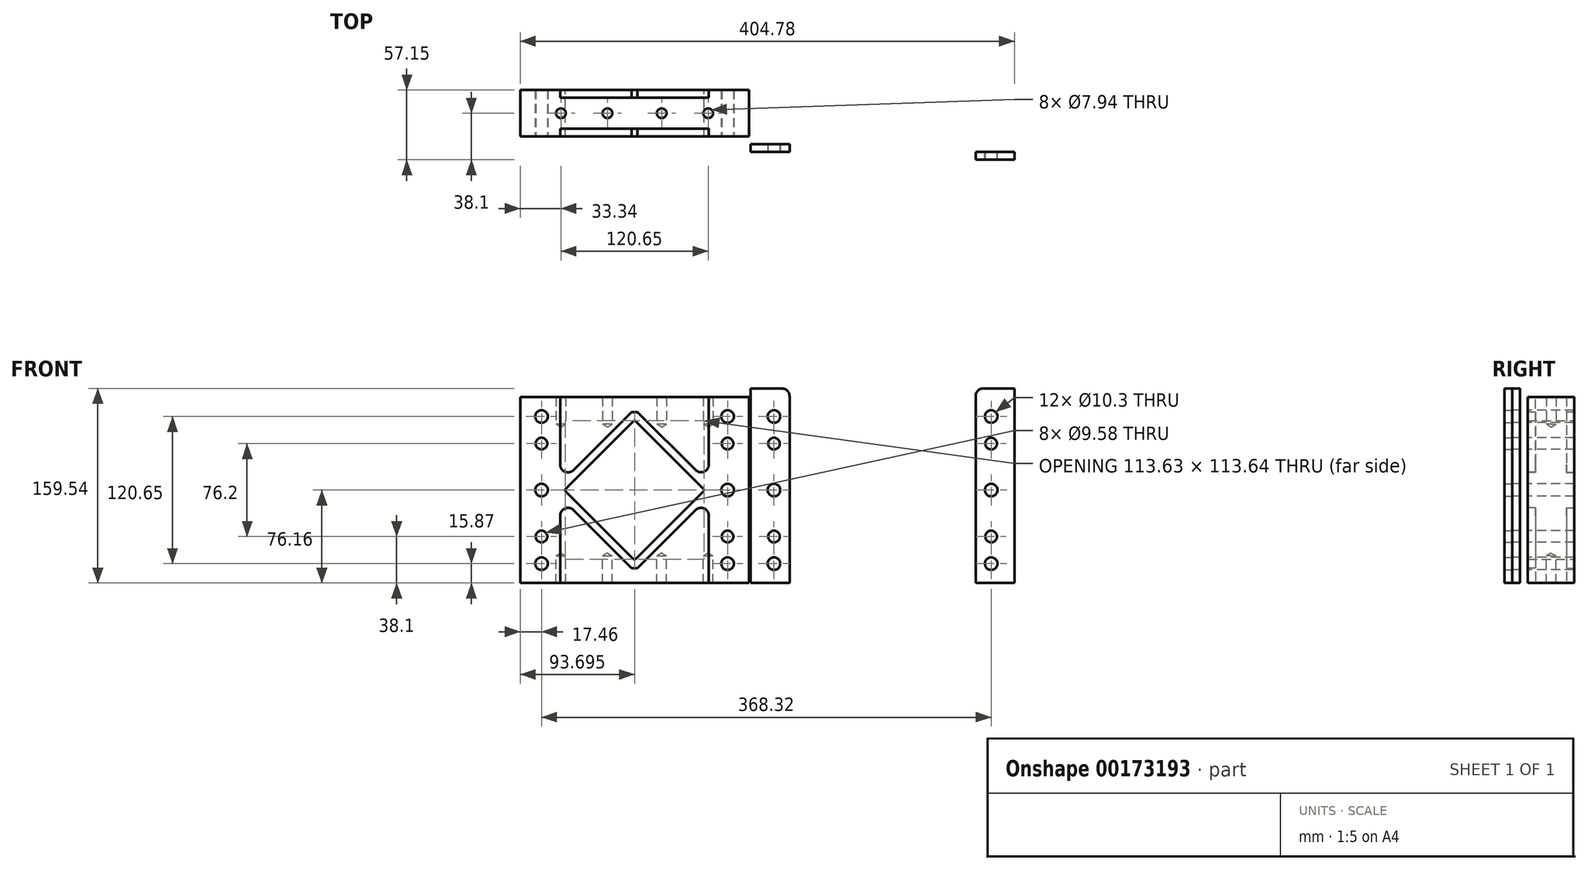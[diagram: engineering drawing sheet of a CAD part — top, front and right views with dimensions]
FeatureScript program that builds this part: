
annotation { "Feature Type Name" : "Feature", "Feature Type Description" : "" }
export const myFeature = defineFeature(function(context is Context, id is Id, definition is map)
    precondition{}
    {
        {
            var Q0;
            Q0=qCreatedBy(makeId("Front.planeOp"),FACE);
            var sketch = newSketch(context, id + "F0", { "sketchPlane" : qUnion([Q0])});
            skLineSegment(sketch, "E0.bottom", {"start": v(-76.3, 64.06) * mm, "end": v(111.02, 64.06) * mm});
            skLineSegment(sketch, "E0.top", {"start": v(-76.3, -88.34) * mm, "end": v(111.02, -88.34) * mm});
            skLineSegment(sketch, "E0.left", {"start": v(-76.3, 64.06) * mm, "end": v(-76.3, -88.34) * mm});
            skLineSegment(sketch, "E0.right", {"start": v(111.02, 64.06) * mm, "end": v(111.02, -88.34) * mm});
            skPoint(sketch, "E1", {"position": v(-58.84, -12.14) * mm});
            skPoint(sketch, "E2", {"position": v(-58.84, -50.24) * mm});
            skPoint(sketch, "E3", {"position": v(-58.84, -72.47) * mm});
            skPoint(sketch, "E4", {"position": v(-58.84, 25.96) * mm});
            skPoint(sketch, "E5", {"position": v(-58.84, 48.18) * mm});
            skPoint(sketch, "E6", {"position": v(93.56, 48.18) * mm});
            skPoint(sketch, "E7", {"position": v(93.56, 25.96) * mm});
            skPoint(sketch, "E8", {"position": v(93.56, -12.14) * mm});
            skPoint(sketch, "E9", {"position": v(93.56, -50.24) * mm});
            skPoint(sketch, "E10", {"position": v(93.56, -72.47) * mm});
            skPoint(sketch, "E11", {"position": v(17.4, -12.18) * mm});
            skLineSegment(sketch, "E12.0", {"start": v(73.75, -13.3) * mm, "end": v(18.52, -68.53) * mm});
            skLineSegment(sketch, "E13.0", {"start": v(-38.96, -13.3) * mm, "end": v(16.27, -68.53) * mm});
            skLineSegment(sketch, "E14.0", {"start": v(18.52, 44.17) * mm, "end": v(73.75, -11.06) * mm});
            skLineSegment(sketch, "E15.trimOffspring", {"start": v(16.27, 44.17) * mm, "end": v(-38.96, -11.06) * mm});
            skPoint(sketch, "E16.visualSharp", {"position": v(17.4, 45.3) * mm});
            skArc(sketch, "E16.filletArc", {"start": v(18.52, 44.17) * mm, "mid": v(17.4, 44.64) * mm, "end": v(16.27, 44.17) * mm});
            skPoint(sketch, "E17.visualSharp", {"position": v(74.87, -12.18) * mm});
            skArc(sketch, "E17.filletArc", {"start": v(73.75, -13.3) * mm, "mid": v(74.21, -12.18) * mm, "end": v(73.75, -11.06) * mm});
            skPoint(sketch, "E18.visualSharp", {"position": v(17.4, -69.65) * mm});
            skArc(sketch, "E18.filletArc", {"start": v(16.27, -68.53) * mm, "mid": v(17.4, -69) * mm, "end": v(18.52, -68.53) * mm});
            skPoint(sketch, "E19.visualSharp", {"position": v(-40.08, -12.18) * mm});
            skArc(sketch, "E19.filletArc", {"start": v(-38.96, -11.06) * mm, "mid": v(-39.42, -12.18) * mm, "end": v(-38.96, -13.3) * mm});
            skSolve(sketch);
        }
        {
            var Q0;
            Q0=makeQuery(id+"F0.imprint","IMPRINT",FACE,{"disambiguationData":[TD([[makeQuery(id+"F0.imprint","IMPRINT",EDGE,{"derivedFrom":sQuery(id+"F0.wireOp",EDGE,"E0.bottom")}),-1.0]])]});
            extrude(context, id + "F1", {"entities" : qUnion([Q0]), "depth" : 38.1 * mm});
        }
        {
            var Q0;
            Q0=makeQuery(id+"F1.opExtrude","CAP_FACE",FACE,{"disambiguationData":[OSD([sQuery(id+"F0.wireOp",EDGE,"E0.bottom"),sQuery(id+"F0.wireOp",EDGE,"E0.top"),sQuery(id+"F0.wireOp",EDGE,"E0.left"),sQuery(id+"F0.wireOp",EDGE,"E0.right"),sQuery(id+"F0.wireOp",EDGE,"9NI2HCdm-zhV7-IXKU-Ilw0-qgHgseYNw8uk"),sQuery(id+"F0.wireOp",EDGE,"780ab442-0033-43c3-96a2-e75c31360361"),sQuery(id+"F0.wireOp",EDGE,"ca78d6b7-7b32-4318-8b30-639c1e3c6c27"),sQuery(id+"F0.wireOp",EDGE,"23cbe407-0eed-4e64-8f3f-165a4f1e2653"),sQuery(id+"F0.wireOp",EDGE,"2d58fa3e-12f2-48dd-afb8-51d7db77980c"),sQuery(id+"F0.wireOp",EDGE,"b4ce7634-13e8-413b-b57b-a0738a6edea7"),sQuery(id+"F0.wireOp",EDGE,"E12.0"),sQuery(id+"F0.wireOp",EDGE,"E13.0"),sQuery(id+"F0.wireOp",EDGE,"E14.0"),sQuery(id+"F0.wireOp",EDGE,"E15.trimOffspring"),sQuery(id+"F0.wireOp",EDGE,"E16.filletArc"),sQuery(id+"F0.wireOp",EDGE,"E17.filletArc"),sQuery(id+"F0.wireOp",EDGE,"E18.filletArc"),sQuery(id+"F0.wireOp",EDGE,"E19.filletArc")])],"isStart":false});
            var sketch = newSketch(context, id + "F2", { "sketchPlane" : qUnion([Q0])});
            skLineSegment(sketch, "E20.0", {"start": v(14.96, 51.84) * mm, "end": v(-32.67, 4.2) * mm});
            skLineSegment(sketch, "E21.0", {"start": v(19.83, 51.84) * mm, "end": v(67.4, 4.28) * mm});
            skLineSegment(sketch, "E22.0", {"start": v(67.4, -28.63) * mm, "end": v(19.83, -76.2) * mm});
            skLineSegment(sketch, "E23.0", {"start": v(-32.67, -28.56) * mm, "end": v(14.96, -76.2) * mm});
            skLineSegment(sketch, "E24", {"start": v(78.24, 8.77) * mm, "end": v(78.24, 64.06) * mm});
            skLineSegment(sketch, "E25", {"start": v(78.24, -33.12) * mm, "end": v(78.24, -88.34) * mm});
            skLineSegment(sketch, "E26", {"start": v(-76.3, -12.14) * mm, "end": v(111.02, -12.14) * mm});
            skLineSegment(sketch, "E27", {"start": v(17.36, -12.14) * mm, "end": v(17.35, -88.34) * mm});
            skLineSegment(sketch, "E28", {"start": v(17.36, -12.14) * mm, "end": v(17.36, 64.06) * mm});
            skLineSegment(sketch, "E29.MirrorCS", {"start": v(-43.51, 8.7) * mm, "end": v(-43.51, 64.06) * mm});
            skLineSegment(sketch, "E30.MirrorCS", {"start": v(-43.51, -33.05) * mm, "end": v(-43.51, -88.34) * mm});
            skPoint(sketch, "E31.newPointB", {"position": v(-43.51, -6.56) * mm});
            skArc(sketch, "E31.filletArc", {"start": v(-43.51, 8.7) * mm, "mid": v(-39.6, 2.83) * mm, "end": v(-32.67, 4.2) * mm});
            skPoint(sketch, "E32.newPointB", {"position": v(-43.51, -17.8) * mm});
            skArc(sketch, "E32.filletArc", {"start": v(-32.67, -28.56) * mm, "mid": v(-39.6, -27.19) * mm, "end": v(-43.51, -33.05) * mm});
            skPoint(sketch, "E33.visualSharp", {"position": v(78.24, -17.8) * mm});
            skArc(sketch, "E33.filletArc", {"start": v(78.24, -33.12) * mm, "mid": v(74.32, -27.25) * mm, "end": v(67.4, -28.63) * mm});
            skLineSegment(sketch, "E34.0", {"start": v(14.96, 51.84) * mm, "end": v(19.83, 51.84) * mm});
            skPoint(sketch, "E35.orphan", {"position": v(23, 48.66) * mm});
            skLineSegment(sketch, "E36.0", {"start": v(19.83, -76.2) * mm, "end": v(14.96, -76.2) * mm});
            skPoint(sketch, "E37.visualSharp", {"position": v(78.24, -6.56) * mm});
            skArc(sketch, "E37.filletArc", {"start": v(67.4, 4.28) * mm, "mid": v(74.32, 2.9) * mm, "end": v(78.24, 8.77) * mm});
            skLineSegment(sketch, "E38", {"start": v(19.83, 51.84) * mm, "end": v(14.96, 51.84) * mm});
            skLineSegment(sketch, "E39", {"start": v(14.96, -76.2) * mm, "end": v(19.83, -76.2) * mm});
            skSolve(sketch);
        }
        {
            var Q0;
            Q0=sQuery(id+"F0.wireOp",VERTEX,"E4");
            var Q1;
            Q1=sQuery(id+"F0.wireOp",VERTEX,"E2");
            var Q2;
            Q2=sQuery(id+"F0.wireOp",VERTEX,"E9");
            var Q3;
            Q3=sQuery(id+"F0.wireOp",VERTEX,"E7");
            var Q4;
            Q4=makeQuery(id+"F1.opExtrude","SWEPT_BODY",BODY,{"disambiguationData":[OSD([sQuery(id+"F0.wireOp",EDGE,"E0.bottom"),sQuery(id+"F0.wireOp",EDGE,"E0.top"),sQuery(id+"F0.wireOp",EDGE,"E0.left"),sQuery(id+"F0.wireOp",EDGE,"E0.right"),sQuery(id+"F0.wireOp",EDGE,"9NI2HCdm-zhV7-IXKU-Ilw0-qgHgseYNw8uk"),sQuery(id+"F0.wireOp",EDGE,"780ab442-0033-43c3-96a2-e75c31360361"),sQuery(id+"F0.wireOp",EDGE,"ca78d6b7-7b32-4318-8b30-639c1e3c6c27"),sQuery(id+"F0.wireOp",EDGE,"23cbe407-0eed-4e64-8f3f-165a4f1e2653"),sQuery(id+"F0.wireOp",EDGE,"2d58fa3e-12f2-48dd-afb8-51d7db77980c"),sQuery(id+"F0.wireOp",EDGE,"b4ce7634-13e8-413b-b57b-a0738a6edea7"),sQuery(id+"F0.wireOp",EDGE,"E12.0"),sQuery(id+"F0.wireOp",EDGE,"E13.0"),sQuery(id+"F0.wireOp",EDGE,"E14.0"),sQuery(id+"F0.wireOp",EDGE,"E15.trimOffspring"),sQuery(id+"F0.wireOp",EDGE,"E16.filletArc"),sQuery(id+"F0.wireOp",EDGE,"E17.filletArc"),sQuery(id+"F0.wireOp",EDGE,"E18.filletArc"),sQuery(id+"F0.wireOp",EDGE,"E19.filletArc")])]});
            hole(context, id + "F3", {"style" : HoleStyle.SIMPLE, "endStyle" : HoleEndStyle.THROUGH, "oppositeDirection" : true, "holeDiameter" : 9.58 * mm, "locations" : qUnion([Q0, Q1, Q2, Q3]), "scope" : qUnion([Q4]), "isTappedThrough" : true});
        }
        {
            var Q0;
            {var subQ6=sQuery(id+"F2.wireOp",EDGE,"E20.0");Q0=makeQuery(id+"F2.imprint","IMPRINT",FACE,{"disambiguationData":[TD([[makeQuery(id+"F2.imprint","IMPRINT",EDGE,{"derivedFrom":subQ6}),-1.0]])]});}
            var Q1;
            {var subQ1=sQuery(id+"F2.wireOp",EDGE,"E21.0");Q1=makeQuery(id+"F2.imprint","IMPRINT",FACE,{"disambiguationData":[TD([[makeQuery(id+"F2.imprint","IMPRINT",EDGE,{"derivedFrom":subQ1}),1.0]])]});}
            var Q2;
            {var subQ6=sQuery(id+"F2.wireOp",EDGE,"E22.0");Q2=makeQuery(id+"F2.imprint","IMPRINT",FACE,{"disambiguationData":[TD([[makeQuery(id+"F2.imprint","IMPRINT",EDGE,{"derivedFrom":subQ6}),1.0]])]});}
            var Q3;
            {var subQ6=sQuery(id+"F2.wireOp",EDGE,"E23.0");Q3=makeQuery(id+"F2.imprint","IMPRINT",FACE,{"disambiguationData":[TD([[makeQuery(id+"F2.imprint","IMPRINT",EDGE,{"derivedFrom":subQ6}),-1.0]])]});}
            extrude(context, id + "F4", {"entities" : qUnion([Q0, Q1, Q2, Q3]), "operationType" : NewBodyOperationType.REMOVE, "oppositeDirection" : true, "depth" : 6.35 * mm});
        }
        {
            var Q0;
            Q0=makeQuery(id+"F0.imprint","IMPRINT",FACE,{"disambiguationData":[TD([[makeQuery(id+"F0.imprint","IMPRINT",EDGE,{"derivedFrom":sQuery(id+"F0.wireOp",EDGE,"E0.bottom")}),-1.0]])]});
            var sketch = newSketch(context, id + "F5", { "sketchPlane" : qUnion([Q0])});
            skLineSegment(sketch, "E40.0", {"start": v(19.76, 51.91) * mm, "end": v(67.4, 4.28) * mm});
            skLineSegment(sketch, "E41.0", {"start": v(15.03, 51.91) * mm, "end": v(-32.67, 4.21) * mm});
            skLineSegment(sketch, "E42.0", {"start": v(-32.67, -28.57) * mm, "end": v(14.97, -76.2) * mm});
            skLineSegment(sketch, "E43.0", {"start": v(67.4, -28.63) * mm, "end": v(19.82, -76.2) * mm});
            skLineSegment(sketch, "E44.0", {"start": v(78.23, 64.06) * mm, "end": v(78.23, 8.77) * mm});
            skLineSegment(sketch, "E45.0", {"start": v(-43.5, 64.06) * mm, "end": v(-43.5, 8.7) * mm});
            skLineSegment(sketch, "E46.0", {"start": v(-76.3, 51.91) * mm, "end": v(-43.5, 51.91) * mm});
            skLineSegment(sketch, "E47.trimOffspring", {"start": v(15.03, 51.91) * mm, "end": v(19.76, 51.91) * mm});
            skLineSegment(sketch, "E48.trimOffspring", {"start": v(14.97, -76.2) * mm, "end": v(19.82, -76.2) * mm});
            skLineSegment(sketch, "E49.trimOffspring", {"start": v(78.23, -76.2) * mm, "end": v(111.02, -76.2) * mm});
            skArc(sketch, "E50.filletArc", {"start": v(67.4, 4.28) * mm, "mid": v(74.31, 2.9) * mm, "end": v(78.23, 8.77) * mm});
            skArc(sketch, "E51.filletArc", {"start": v(-43.5, 8.7) * mm, "mid": v(-39.59, 2.84) * mm, "end": v(-32.67, 4.21) * mm});
            skLineSegment(sketch, "E52", {"start": v(-43.5, 8.7) * mm, "end": v(-43.5, 2.84) * mm});
            skPoint(sketch, "E52.endSnap0", {"position": v(-39.59, 2.84) * mm});
            skLineSegment(sketch, "E53", {"start": v(78.23, -33.12) * mm, "end": v(78.23, -90.42) * mm});
            skLineSegment(sketch, "E54", {"start": v(-43.5, -33.06) * mm, "end": v(-43.5, -90.42) * mm});
            skPoint(sketch, "E55.newPointB", {"position": v(78.23, 8.77) * mm});
            skArc(sketch, "E55.filletArc", {"start": v(78.23, -33.12) * mm, "mid": v(74.31, -27.26) * mm, "end": v(67.4, -28.63) * mm});
            skArc(sketch, "E56.filletArc", {"start": v(-32.67, -28.57) * mm, "mid": v(-39.59, -27.2) * mm, "end": v(-43.5, -33.06) * mm});
            skSolve(sketch);
        }
        {
            var Q0;
            Q0=makeQuery(id+"F5.imprint","IMPRINT",FACE,{"disambiguationData":[TD([[makeQuery(id+"F5.imprint","IMPRINT",EDGE,{"derivedFrom":sQuery(id+"F5.wireOp",EDGE,"E42.0")}),-1.0]])]});
            var Q1;
            Q1=makeQuery(id+"F5.imprint","IMPRINT",FACE,{"disambiguationData":[TD([[makeQuery(id+"F5.imprint","IMPRINT",EDGE,{"derivedFrom":sQuery(id+"F5.wireOp",EDGE,"E40.0")}),1.0]])]});
            extrude(context, id + "F6", {"entities" : qUnion([Q0, Q1]), "operationType" : NewBodyOperationType.REMOVE, "depth" : 6.35 * mm});
        }
        {
            var Q0;
            Q0=makeQuery(id+"F1.opExtrude","SWEPT_FACE",FACE,{"disambiguationData":[OSD([sQuery(id+"F0.wireOp",EDGE,"E0.top")])]});
            var sketch = newSketch(context, id + "F7", { "sketchPlane" : qUnion([Q0])});
            skLineSegment(sketch, "E57", {"start": v(-76.3, 19.05) * mm, "end": v(111.02, 19.05) * mm});
            skPoint(sketch, "E58.endSnap0", {"position": v(17.36, 31.75) * mm});
            skLineSegment(sketch, "E59", {"start": v(17.36, 6.35) * mm, "end": v(17.36, 31.75) * mm});
            skLineSegment(sketch, "E60.0", {"start": v(39.59, 6.35) * mm, "end": v(39.59, 31.75) * mm});
            skLineSegment(sketch, "E61.0", {"start": v(-4.86, 6.35) * mm, "end": v(-4.86, 31.75) * mm});
            skLineSegment(sketch, "E62.0", {"start": v(77.69, 6.35) * mm, "end": v(77.69, 31.75) * mm});
            skLineSegment(sketch, "E63.0", {"start": v(71.88, -6.35) * mm, "end": v(71.88, 0) * mm});
            skLineSegment(sketch, "E63.1", {"start": v(-82.65, 44.45) * mm, "end": v(-37.16, 44.45) * mm});
            skLineSegment(sketch, "E63.2", {"start": v(-82.65, -6.35) * mm, "end": v(-82.65, 44.45) * mm});
            skLineSegment(sketch, "E63.3", {"start": v(-37.16, -6.35) * mm, "end": v(-82.65, -6.35) * mm});
            skLineSegment(sketch, "E63.4", {"start": v(-37.16, 0) * mm, "end": v(-37.16, -6.35) * mm});
            skLineSegment(sketch, "E63.5", {"start": v(-37.16, 44.45) * mm, "end": v(-37.16, 38.1) * mm});
            skLineSegment(sketch, "E63.6", {"start": v(71.88, 0) * mm, "end": v(-37.16, 0) * mm});
            skLineSegment(sketch, "E63.7", {"start": v(-37.16, 38.1) * mm, "end": v(71.89, 38.1) * mm});
            skLineSegment(sketch, "E63.8", {"start": v(71.89, 38.1) * mm, "end": v(71.89, 44.45) * mm});
            skLineSegment(sketch, "E63.9", {"start": v(71.89, 44.45) * mm, "end": v(117.37, 44.45) * mm});
            skLineSegment(sketch, "E63.10", {"start": v(117.37, 44.45) * mm, "end": v(117.37, -6.35) * mm});
            skLineSegment(sketch, "E63.11", {"start": v(117.37, -6.35) * mm, "end": v(71.88, -6.35) * mm});
            skLineSegment(sketch, "E64.0", {"start": v(-42.96, 6.35) * mm, "end": v(-42.96, 31.75) * mm});
            skPoint(sketch, "E65", {"position": v(-42.96, 19.05) * mm});
            skPoint(sketch, "E66", {"position": v(-4.86, 19.05) * mm});
            skPoint(sketch, "E67", {"position": v(39.59, 19.05) * mm});
            skPoint(sketch, "E68", {"position": v(77.69, 19.05) * mm});
            skSolve(sketch);
        }
        {
            var Q0;
            Q0=sQuery(id+"F7.wireOp",VERTEX,"E65");
            var Q1;
            Q1=sQuery(id+"F7.wireOp",VERTEX,"E66");
            var Q2;
            Q2=sQuery(id+"F7.wireOp",VERTEX,"E68");
            var Q3;
            Q3=sQuery(id+"F7.wireOp",VERTEX,"E67");
            var Q4;
            Q4=makeQuery(id+"F1.opExtrude","SWEPT_BODY",BODY,{"disambiguationData":[OSD([sQuery(id+"F0.wireOp",EDGE,"E0.bottom"),sQuery(id+"F0.wireOp",EDGE,"E0.top"),sQuery(id+"F0.wireOp",EDGE,"E0.left"),sQuery(id+"F0.wireOp",EDGE,"E0.right"),sQuery(id+"F0.wireOp",EDGE,"9NI2HCdm-zhV7-IXKU-Ilw0-qgHgseYNw8uk"),sQuery(id+"F0.wireOp",EDGE,"780ab442-0033-43c3-96a2-e75c31360361"),sQuery(id+"F0.wireOp",EDGE,"ca78d6b7-7b32-4318-8b30-639c1e3c6c27"),sQuery(id+"F0.wireOp",EDGE,"23cbe407-0eed-4e64-8f3f-165a4f1e2653"),sQuery(id+"F0.wireOp",EDGE,"2d58fa3e-12f2-48dd-afb8-51d7db77980c"),sQuery(id+"F0.wireOp",EDGE,"b4ce7634-13e8-413b-b57b-a0738a6edea7"),sQuery(id+"F0.wireOp",EDGE,"E12.0"),sQuery(id+"F0.wireOp",EDGE,"E13.0"),sQuery(id+"F0.wireOp",EDGE,"E14.0"),sQuery(id+"F0.wireOp",EDGE,"E15.trimOffspring"),sQuery(id+"F0.wireOp",EDGE,"E16.filletArc"),sQuery(id+"F0.wireOp",EDGE,"E17.filletArc"),sQuery(id+"F0.wireOp",EDGE,"E18.filletArc"),sQuery(id+"F0.wireOp",EDGE,"E19.filletArc")])]});
            hole(context, id + "F8", {"style" : HoleStyle.SIMPLE, "endStyle" : HoleEndStyle.BLIND, "holeDiameter" : 7.94 * mm, "holeDepth" : 22.22 * mm, "locations" : qUnion([Q0, Q1, Q2, Q3]), "scope" : qUnion([Q4])});
        }
        {
            var Q0;
            Q0=makeQuery(id+"F1.opExtrude","SWEPT_FACE",FACE,{"disambiguationData":[OSD([sQuery(id+"F0.wireOp",EDGE,"E0.bottom")])]});
            var sketch = newSketch(context, id + "F9", { "sketchPlane" : qUnion([Q0])});
            skLineSegment(sketch, "E69", {"start": v(-76.3, -19.05) * mm, "end": v(111.02, -19.05) * mm});
            skLineSegment(sketch, "E70", {"start": v(17.36, -30.06) * mm, "end": v(17.36, -6.35) * mm});
            skPoint(sketch, "E70.startSnap0", {"position": v(17.36, -31.75) * mm});
            skLineSegment(sketch, "E71", {"start": v(39.59, -6.35) * mm, "end": v(39.59, -31.75) * mm});
            skLineSegment(sketch, "E72", {"start": v(-4.86, -6.35) * mm, "end": v(-4.86, -31.75) * mm});
            skLineSegment(sketch, "E73", {"start": v(77.69, -6.35) * mm, "end": v(77.69, -31.75) * mm});
            skLineSegment(sketch, "E74", {"start": v(-42.96, -31.75) * mm, "end": v(-42.96, -6.35) * mm});
            skPoint(sketch, "E75", {"position": v(77.69, -19.05) * mm});
            skPoint(sketch, "E76", {"position": v(39.59, -19.05) * mm});
            skPoint(sketch, "E77", {"position": v(-4.86, -19.05) * mm});
            skPoint(sketch, "E78", {"position": v(-42.96, -19.05) * mm});
            skSolve(sketch);
        }
        {
            var Q0;
            Q0=sQuery(id+"F9.wireOp",VERTEX,"E78");
            var Q1;
            Q1=sQuery(id+"F9.wireOp",VERTEX,"E77");
            var Q2;
            Q2=sQuery(id+"F9.wireOp",VERTEX,"E76");
            var Q3;
            Q3=sQuery(id+"F9.wireOp",VERTEX,"E75");
            var Q4;
            Q4=makeQuery(id+"F1.opExtrude","SWEPT_BODY",BODY,{"disambiguationData":[OSD([sQuery(id+"F0.wireOp",EDGE,"E0.bottom"),sQuery(id+"F0.wireOp",EDGE,"E0.top"),sQuery(id+"F0.wireOp",EDGE,"E0.left"),sQuery(id+"F0.wireOp",EDGE,"E0.right"),sQuery(id+"F0.wireOp",EDGE,"9NI2HCdm-zhV7-IXKU-Ilw0-qgHgseYNw8uk"),sQuery(id+"F0.wireOp",EDGE,"780ab442-0033-43c3-96a2-e75c31360361"),sQuery(id+"F0.wireOp",EDGE,"ca78d6b7-7b32-4318-8b30-639c1e3c6c27"),sQuery(id+"F0.wireOp",EDGE,"23cbe407-0eed-4e64-8f3f-165a4f1e2653"),sQuery(id+"F0.wireOp",EDGE,"2d58fa3e-12f2-48dd-afb8-51d7db77980c"),sQuery(id+"F0.wireOp",EDGE,"b4ce7634-13e8-413b-b57b-a0738a6edea7"),sQuery(id+"F0.wireOp",EDGE,"E12.0"),sQuery(id+"F0.wireOp",EDGE,"E13.0"),sQuery(id+"F0.wireOp",EDGE,"E14.0"),sQuery(id+"F0.wireOp",EDGE,"E15.trimOffspring"),sQuery(id+"F0.wireOp",EDGE,"E16.filletArc"),sQuery(id+"F0.wireOp",EDGE,"E17.filletArc"),sQuery(id+"F0.wireOp",EDGE,"E18.filletArc"),sQuery(id+"F0.wireOp",EDGE,"E19.filletArc")])]});
            hole(context, id + "F10", {"style" : HoleStyle.SIMPLE, "endStyle" : HoleEndStyle.BLIND, "holeDiameter" : 7.94 * mm, "holeDepth" : 22.22 * mm, "locations" : qUnion([Q0, Q1, Q2, Q3]), "scope" : qUnion([Q4])});
        }
        {
            var Q0;
            Q0=sQuery(id+"F0.wireOp",VERTEX,"E3");
            var Q1;
            Q1=sQuery(id+"F0.wireOp",VERTEX,"E1");
            var Q2;
            Q2=sQuery(id+"F0.wireOp",VERTEX,"E5");
            var Q3;
            Q3=sQuery(id+"F0.wireOp",VERTEX,"E6");
            var Q4;
            Q4=sQuery(id+"F0.wireOp",VERTEX,"E8");
            var Q5;
            Q5=sQuery(id+"F0.wireOp",VERTEX,"E10");
            var Q6;
            Q6=makeQuery(id+"F1.opExtrude","SWEPT_BODY",BODY,{"disambiguationData":[OSD([sQuery(id+"F0.wireOp",EDGE,"E0.bottom"),sQuery(id+"F0.wireOp",EDGE,"E0.top"),sQuery(id+"F0.wireOp",EDGE,"E0.left"),sQuery(id+"F0.wireOp",EDGE,"E0.right"),sQuery(id+"F0.wireOp",EDGE,"E12.0"),sQuery(id+"F0.wireOp",EDGE,"E13.0"),sQuery(id+"F0.wireOp",EDGE,"E14.0"),sQuery(id+"F0.wireOp",EDGE,"E15.trimOffspring"),sQuery(id+"F0.wireOp",EDGE,"E16.filletArc"),sQuery(id+"F0.wireOp",EDGE,"E17.filletArc"),sQuery(id+"F0.wireOp",EDGE,"E18.filletArc"),sQuery(id+"F0.wireOp",EDGE,"E19.filletArc")])]});
            hole(context, id + "F11", {"style" : HoleStyle.SIMPLE, "endStyle" : HoleEndStyle.THROUGH, "oppositeDirection" : true, "holeDiameter" : 10.3 * mm, "locations" : qUnion([Q0, Q1, Q2, Q3, Q4, Q5]), "scope" : qUnion([Q6]), "isTappedThrough" : true});
        }
        {
            var Q0;
            Q0=makeQuery(id+"F1.opExtrude","CAP_FACE",FACE,{"disambiguationData":[OSD([sQuery(id+"F0.wireOp",EDGE,"E0.bottom"),sQuery(id+"F0.wireOp",EDGE,"E0.top"),sQuery(id+"F0.wireOp",EDGE,"E0.left"),sQuery(id+"F0.wireOp",EDGE,"E0.right"),sQuery(id+"F0.wireOp",EDGE,"E12.0"),sQuery(id+"F0.wireOp",EDGE,"E13.0"),sQuery(id+"F0.wireOp",EDGE,"E14.0"),sQuery(id+"F0.wireOp",EDGE,"E15.trimOffspring"),sQuery(id+"F0.wireOp",EDGE,"E16.filletArc"),sQuery(id+"F0.wireOp",EDGE,"E17.filletArc"),sQuery(id+"F0.wireOp",EDGE,"E18.filletArc"),sQuery(id+"F0.wireOp",EDGE,"E19.filletArc")])],"isStart":false});
            var sketch = newSketch(context, id + "F12", { "sketchPlane" : qUnion([Q0])});
            skLineSegment(sketch, "E79", {"start": v(17.4, 51.84) * mm, "end": v(17.4, -69) * mm});
            skLineSegment(sketch, "E80.0", {"start": v(17.3, 51.84) * mm, "end": v(17.3, -69) * mm});
            skLineSegment(sketch, "E81.0", {"start": v(-46.2, 51.84) * mm, "end": v(-46.2, -69) * mm});
            skLineSegment(sketch, "E82.0", {"start": v(80.8, 51.84) * mm, "end": v(80.8, -69) * mm});
            skLineSegment(sketch, "E83.top", {"start": v(87.16, 71.2) * mm, "end": v(112.56, 71.2) * mm});
            skLineSegment(sketch, "E83.left", {"start": v(80.8, -8.58) * mm, "end": v(80.8, 64.85) * mm});
            skLineSegment(sketch, "E83.right", {"start": v(112.56, -8.58) * mm, "end": v(112.56, 71.2) * mm});
            skLineSegment(sketch, "E84.top", {"start": v(80.8, -88.34) * mm, "end": v(112.56, -88.34) * mm});
            skLineSegment(sketch, "E84.left", {"start": v(80.8, -8.58) * mm, "end": v(80.8, -88.34) * mm});
            skLineSegment(sketch, "E84.right", {"start": v(112.56, -8.58) * mm, "end": v(112.56, -88.34) * mm});
            skPoint(sketch, "E85.visualSharp", {"position": v(80.8, 71.2) * mm});
            skArc(sketch, "E85.filletArc", {"start": v(87.16, 71.2) * mm, "mid": v(82.67, 69.34) * mm, "end": v(80.8, 64.85) * mm});
            skSolve(sketch);
        }
        {
            var Q0;
            {var subQ0=sQuery(id+"F0.wireOp",EDGE,"E0.right");var subQ8=makeQuery(id+"F1.opExtrude","CAP_EDGE",EDGE,{"disambiguationData":[OSD([subQ0])],"isStart":false});Q0=makeQuery(id+"F12.imprint","IMPRINT",FACE,{"disambiguationData":[TD([[makeQuery(id+"F12.imprint","IMPRINT",EDGE,{"derivedFrom":subQ8}),-1.0]])]});}
            var Q1;
            Q1=makeQuery(id+"F12.imprint","IMPRINT",FACE,{"disambiguationData":[TD([[makeQuery(id+"F12.imprint","IMPRINT",EDGE,{"derivedFrom":sQuery(id+"F12.wireOp",EDGE,"E83.top")}),-1.0]])]});
            extrude(context, id + "F13", {"entities" : qUnion([Q0, Q1]), "depth" : 6.35 * mm});
        }
        {
            var Q0;
            Q0=makeQuery(id+"F13.opExtrude","SWEPT_BODY",BODY,{"disambiguationData":[OSD([sQuery(id+"F0.wireOp",EDGE,"E0.bottom"),sQuery(id+"F0.wireOp",EDGE,"E0.top"),sQuery(id+"F0.wireOp",EDGE,"E0.left"),sQuery(id+"F0.wireOp",EDGE,"E0.right"),sQuery(id+"F0.wireOp",EDGE,"E12.0"),sQuery(id+"F0.wireOp",EDGE,"E13.0"),sQuery(id+"F0.wireOp",EDGE,"E14.0"),sQuery(id+"F0.wireOp",EDGE,"E15.trimOffspring"),sQuery(id+"F0.wireOp",EDGE,"E16.filletArc"),sQuery(id+"F0.wireOp",EDGE,"E17.filletArc"),sQuery(id+"F0.wireOp",EDGE,"E18.filletArc"),sQuery(id+"F0.wireOp",EDGE,"E19.filletArc"),sQuery(id+"F3.hole-2.sketch.wireOp",EDGE,"core_line_2"),sQuery(id+"F3.hole-3.sketch.wireOp",EDGE,"core_line_2"),sQuery(id+"F11.hole-3.sketch.wireOp",EDGE,"core_line_2"),sQuery(id+"F11.hole-4.sketch.wireOp",EDGE,"core_line_2"),sQuery(id+"F11.hole-5.sketch.wireOp",EDGE,"core_line_2"),sQuery(id+"F12.wireOp",EDGE,"E83.top"),sQuery(id+"F12.wireOp",EDGE,"E83.left"),sQuery(id+"F12.wireOp",EDGE,"E83.right"),sQuery(id+"F12.wireOp",EDGE,"E84.top"),sQuery(id+"F12.wireOp",EDGE,"E84.left"),sQuery(id+"F12.wireOp",EDGE,"E84.right"),sQuery(id+"F12.wireOp",EDGE,"E85.filletArc")])]});
            var Q1;
            Q1=makeQuery(id+"F13.opExtrude","CAP_EDGE",EDGE,{"disambiguationData":[OSD([sQuery(id+"F12.wireOp",EDGE,"E83.right"),sQuery(id+"F12.wireOp",EDGE,"E84.right")])],"isStart":false});
            transform(context, id + "F14", {"entities" : qUnion([Q0]), "transformType" : TransformType.ROTATION, "transformAxis" : qUnion([Q1]), "angle" : 180 * degree, "makeCopy" : false});
        }
        {
            var Q0;
            Q0=makeQuery(id+"F13.opExtrude","SWEPT_BODY",BODY,{"disambiguationData":[OSD([sQuery(id+"F0.wireOp",EDGE,"E0.bottom"),sQuery(id+"F0.wireOp",EDGE,"E0.top"),sQuery(id+"F0.wireOp",EDGE,"E0.left"),sQuery(id+"F0.wireOp",EDGE,"E0.right"),sQuery(id+"F0.wireOp",EDGE,"E12.0"),sQuery(id+"F0.wireOp",EDGE,"E13.0"),sQuery(id+"F0.wireOp",EDGE,"E14.0"),sQuery(id+"F0.wireOp",EDGE,"E15.trimOffspring"),sQuery(id+"F0.wireOp",EDGE,"E16.filletArc"),sQuery(id+"F0.wireOp",EDGE,"E17.filletArc"),sQuery(id+"F0.wireOp",EDGE,"E18.filletArc"),sQuery(id+"F0.wireOp",EDGE,"E19.filletArc"),sQuery(id+"F3.hole-2.sketch.wireOp",EDGE,"core_line_2"),sQuery(id+"F3.hole-3.sketch.wireOp",EDGE,"core_line_2"),sQuery(id+"F11.hole-3.sketch.wireOp",EDGE,"core_line_2"),sQuery(id+"F11.hole-4.sketch.wireOp",EDGE,"core_line_2"),sQuery(id+"F11.hole-5.sketch.wireOp",EDGE,"core_line_2"),sQuery(id+"F12.wireOp",EDGE,"E83.top"),sQuery(id+"F12.wireOp",EDGE,"E83.left"),sQuery(id+"F12.wireOp",EDGE,"E83.right"),sQuery(id+"F12.wireOp",EDGE,"E84.top"),sQuery(id+"F12.wireOp",EDGE,"E84.left"),sQuery(id+"F12.wireOp",EDGE,"E84.right"),sQuery(id+"F12.wireOp",EDGE,"E85.filletArc")])]});
            transform(context, id + "F15", {"entities" : qUnion([Q0]), "transformType" : TransformType.TRANSLATION_3D, "dx" : 152.4 * mm, "dy" : 0 * mm, "dz" : 0 * mm, "makeCopy" : true});
        }
        {
            var Q0;
            Q0=makeQuery(id+"F15.opPattern","COPY",BODY,{"derivedFrom":makeQuery(id+"F13.opExtrude","SWEPT_BODY",BODY,{"disambiguationData":[OSD([sQuery(id+"F0.wireOp",EDGE,"E0.bottom"),sQuery(id+"F0.wireOp",EDGE,"E0.top"),sQuery(id+"F0.wireOp",EDGE,"E0.left"),sQuery(id+"F0.wireOp",EDGE,"E0.right"),sQuery(id+"F0.wireOp",EDGE,"E12.0"),sQuery(id+"F0.wireOp",EDGE,"E13.0"),sQuery(id+"F0.wireOp",EDGE,"E14.0"),sQuery(id+"F0.wireOp",EDGE,"E15.trimOffspring"),sQuery(id+"F0.wireOp",EDGE,"E16.filletArc"),sQuery(id+"F0.wireOp",EDGE,"E17.filletArc"),sQuery(id+"F0.wireOp",EDGE,"E18.filletArc"),sQuery(id+"F0.wireOp",EDGE,"E19.filletArc"),sQuery(id+"F3.hole-2.sketch.wireOp",EDGE,"core_line_2"),sQuery(id+"F3.hole-3.sketch.wireOp",EDGE,"core_line_2"),sQuery(id+"F11.hole-3.sketch.wireOp",EDGE,"core_line_2"),sQuery(id+"F11.hole-4.sketch.wireOp",EDGE,"core_line_2"),sQuery(id+"F11.hole-5.sketch.wireOp",EDGE,"core_line_2"),sQuery(id+"F12.wireOp",EDGE,"E83.top"),sQuery(id+"F12.wireOp",EDGE,"E83.left"),sQuery(id+"F12.wireOp",EDGE,"E83.right"),sQuery(id+"F12.wireOp",EDGE,"E84.top"),sQuery(id+"F12.wireOp",EDGE,"E84.left"),sQuery(id+"F12.wireOp",EDGE,"E84.right"),sQuery(id+"F12.wireOp",EDGE,"E85.filletArc")])]}),"instanceName":"1"});
            var Q1;
            Q1=makeQuery(id+"F15.opPattern","COPY",EDGE,{"derivedFrom":makeQuery(id+"F13.opExtrude","CAP_EDGE",EDGE,{"disambiguationData":[OSD([sQuery(id+"F12.wireOp",EDGE,"E83.left"),sQuery(id+"F12.wireOp",EDGE,"E84.left")])],"isStart":true}),"instanceName":"1"});
            transform(context, id + "F16", {"entities" : qUnion([Q0]), "transformType" : TransformType.ROTATION, "transformAxis" : qUnion([Q1]), "angle" : 180 * degree, "makeCopy" : false});
        }
    });
